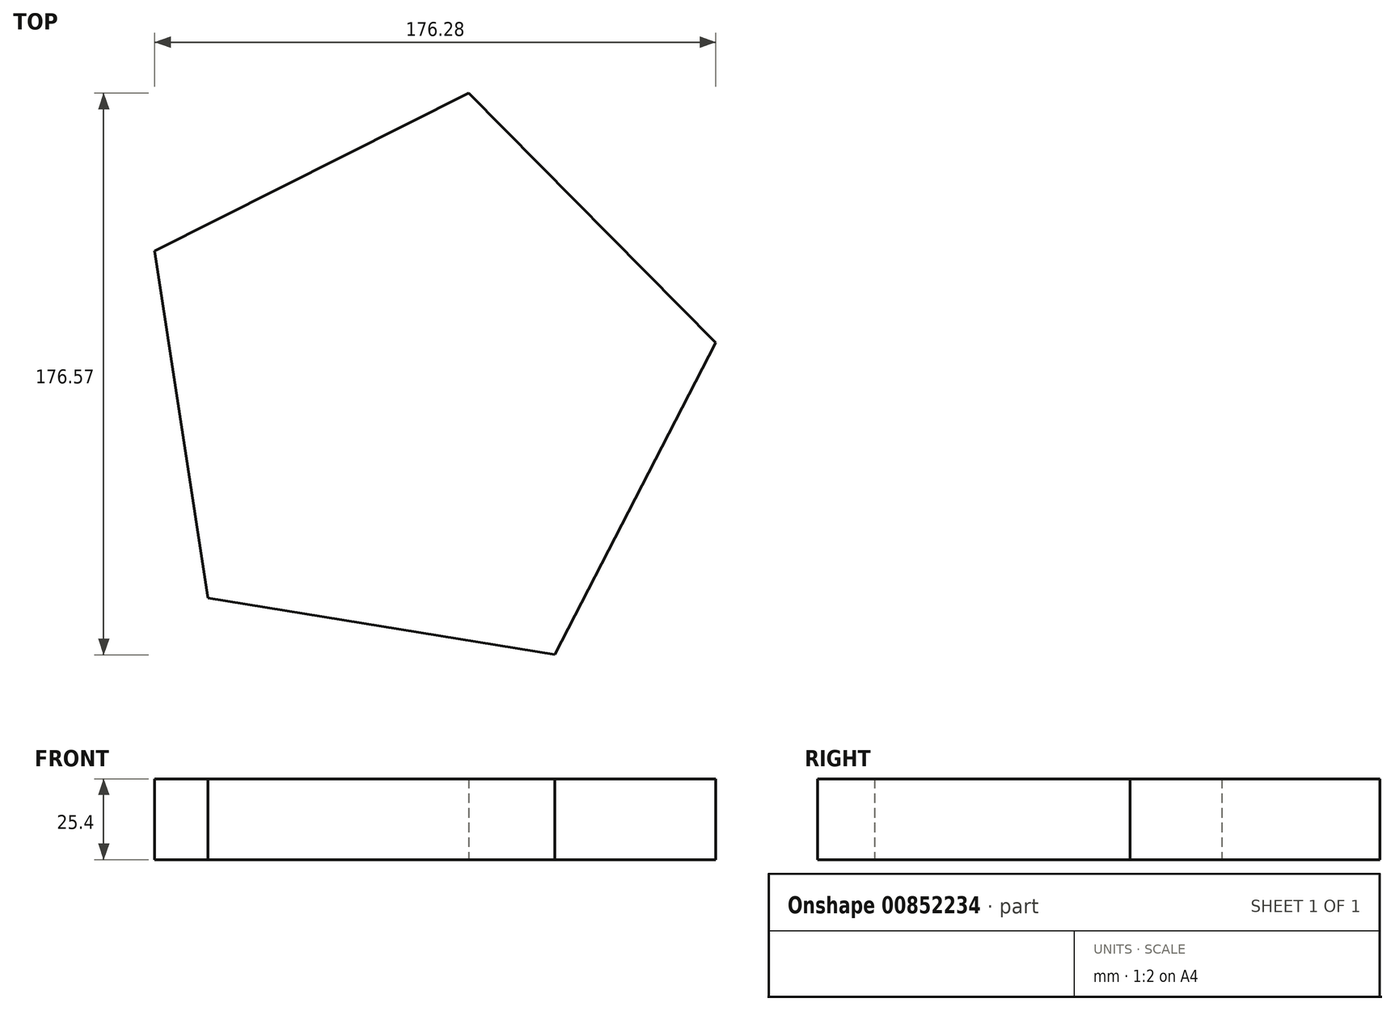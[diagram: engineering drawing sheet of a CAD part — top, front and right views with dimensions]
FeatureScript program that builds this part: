
annotation { "Feature Type Name" : "Feature", "Feature Type Description" : "" }
export const myFeature = defineFeature(function(context is Context, id is Id, definition is map)
    precondition{}
    {
        {
            var Q0;
            Q0=qCreatedBy(makeId("Top.planeOp"),FACE);
            var sketch = newSketch(context, id + "F0", { "sketchPlane" : qUnion([Q0])});
            skCircle(sketch, "E0.cCircle", {"center": v(0, 0) * mm, "radius": 75.97 * mm, "construction": true});
            skLineSegment(sketch, "E0.0", {"start": v(15.16, 92.68) * mm, "end": v(92.82, 14.22) * mm});
            skLineSegment(sketch, "E0.1", {"start": v(92.82, 14.22) * mm, "end": v(42.2, -83.89) * mm});
            skLineSegment(sketch, "E0.2", {"start": v(42.2, -83.89) * mm, "end": v(-66.74, -66.07) * mm});
            skLineSegment(sketch, "E0.3", {"start": v(-66.74, -66.07) * mm, "end": v(-83.46, 43.06) * mm});
            skLineSegment(sketch, "E0.4", {"start": v(-83.46, 43.06) * mm, "end": v(15.16, 92.68) * mm});
            skPoint(sketch, "E0.0.midPoint", {"position": v(54, 53.45) * mm});
            skSolve(sketch);
        }
        {
            var Q0;
            Q0 = qSketchRegion(id + "F0", true);
            var sketch = newSketch(context, id + "F1", { "sketchPlane" : qUnion([Q0])});
            skSolve(sketch);
        }
        {
            var Q0;
            Q0=makeQuery(id+"F1.imprint","IMPRINT",FACE,{"disambiguationData":[TD([[makeQuery(id+"F1.imprint","IMPRINT",EDGE,{"derivedFrom":makeQuery(id+"F0.imprint","IMPRINT",EDGE,{"derivedFrom":sQuery(id+"F0.wireOp",EDGE,"E0.0")})}),-1.0]])]});
            extrude(context, id + "F2", {"entities" : qUnion([Q0]), "depth" : 25.4 * mm, "offsetDistance" : 25.4 * mm});
        }
    });
